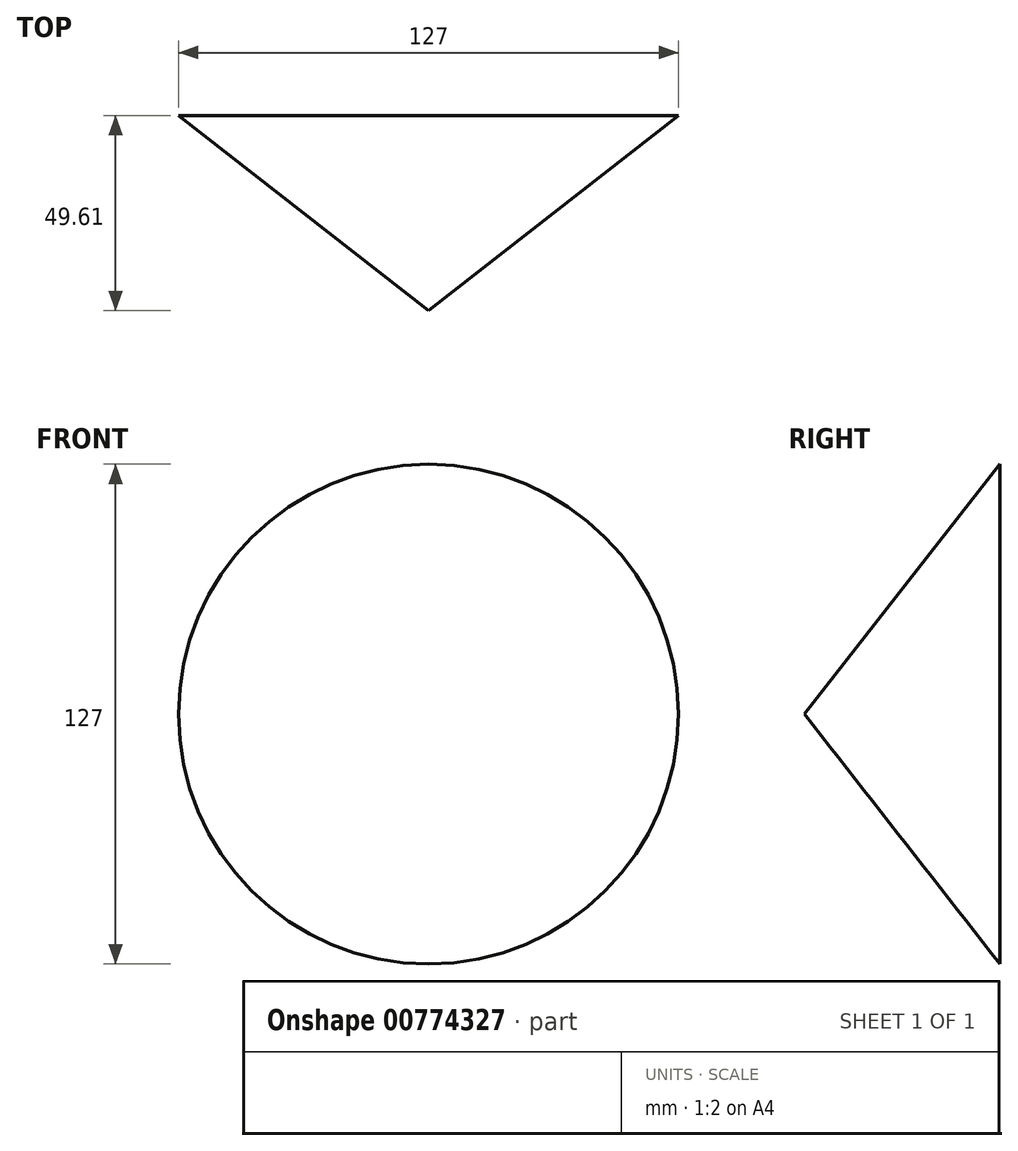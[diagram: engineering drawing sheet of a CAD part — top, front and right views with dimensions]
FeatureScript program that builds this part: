
annotation { "Feature Type Name" : "Feature", "Feature Type Description" : "" }
export const myFeature = defineFeature(function(context is Context, id is Id, definition is map)
    precondition{}
    {
        {
            var Q0;
            Q0=qCreatedBy(makeId("Front.planeOp"),FACE);
            var sketch = newSketch(context, id + "F0", { "sketchPlane" : qUnion([Q0])});
            skCircle(sketch, "E0", {"center": v(0, 0) * mm, "radius": 63.5 * mm});
            skSolve(sketch);
        }
        {
            var Q0;
            Q0=makeQuery(id+"F0.imprint","IMPRINT",FACE,{"disambiguationData":[TD([[makeQuery(id+"F0.imprint","IMPRINT",EDGE,{"derivedFrom":sQuery(id+"F0.wireOp",EDGE,"E0")}),1.0]])]});
            extrude(context, id + "F1", {"entities" : qUnion([Q0]), "depth" : 50 * mm, "offsetDistance" : 25.4 * mm, "hasDraft" : true, "draftAngle" : 52 * degree, "draftPullDirection" : true});
        }
    });
